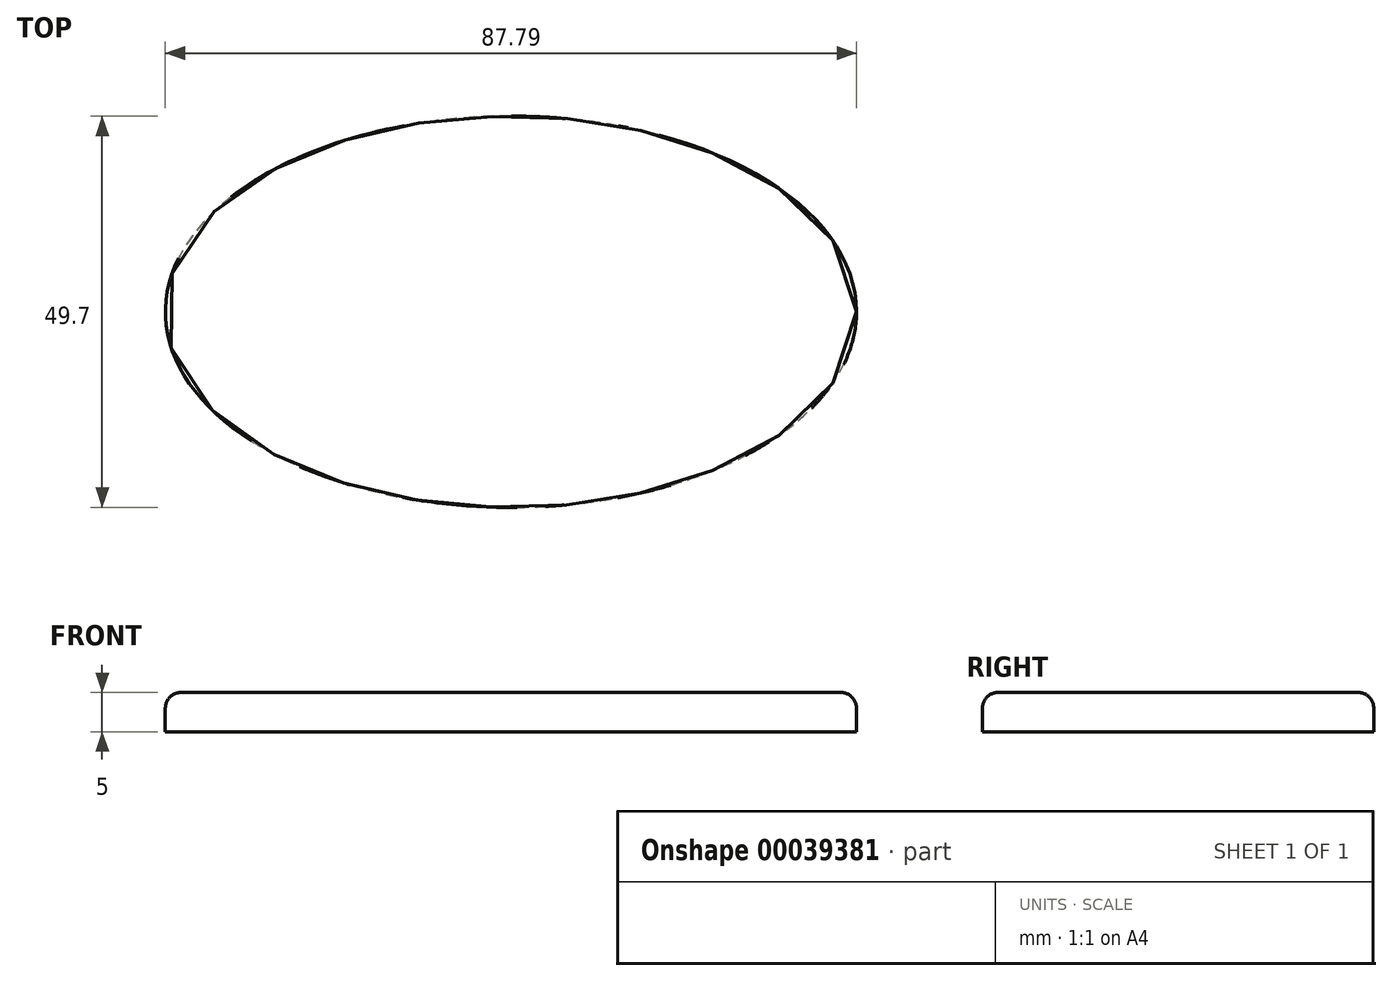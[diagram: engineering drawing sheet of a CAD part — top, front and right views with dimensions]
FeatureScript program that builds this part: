
annotation { "Feature Type Name" : "Feature", "Feature Type Description" : "" }
export const myFeature = defineFeature(function(context is Context, id is Id, definition is map)
    precondition{}
    {
        {
            var Q0;
            Q0=qCreatedBy(makeId("Top.planeOp"),FACE);
            var sketch = newSketch(context, id + "F0", { "sketchPlane" : qUnion([Q0])});
            skEllipse(sketch, "E0", {"center": v(-26.61, 19.76) * mm, "majorRadius": 43.9 * mm, "minorRadius": 24.85 * mm, "majorAxis": v(1, 0)});
            skSolve(sketch);
        }
        {
            var Q0;
            Q0=makeQuery(id+"F0.imprint","IMPRINT",FACE,{"disambiguationData":[TD([[makeQuery(id+"F0.imprint","IMPRINT",EDGE,{"derivedFrom":sQuery(id+"F0.wireOp",EDGE,"E0")}),1.0]])]});
            extrude(context, id + "F1", {"entities" : qUnion([Q0]), "depth" : 5 * mm});
        }
        {
            var Q0;
            Q0=makeQuery(id+"F1.opExtrude","CAP_FACE",FACE,{"disambiguationData":[OSD([sQuery(id+"F0.wireOp",EDGE,"E0")])],"isStart":false});
            fillet(context, id + "F2", {"entities" : qUnion([Q0]), "radius" : 2 * mm, "allowEdgeOverflow" : false});
        }
    });
